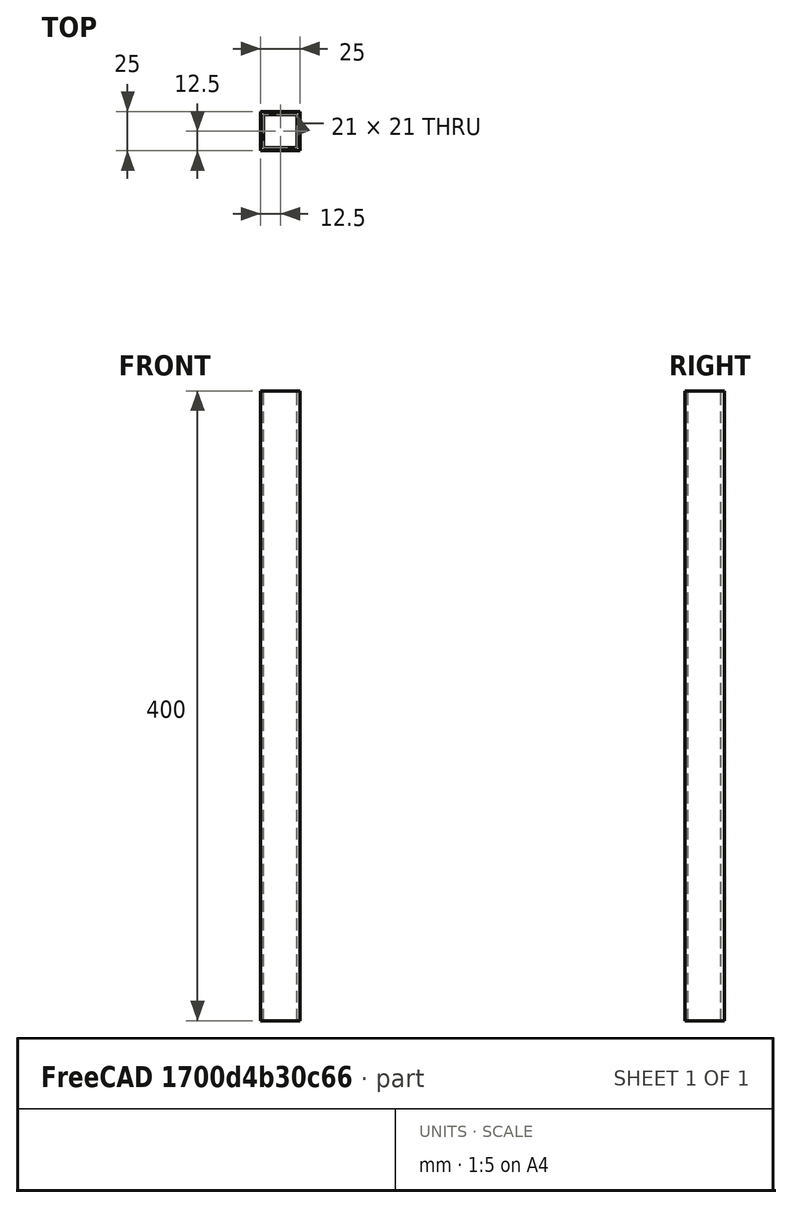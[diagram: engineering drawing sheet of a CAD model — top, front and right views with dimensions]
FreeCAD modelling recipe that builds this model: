
FCSTD DOCUMENT  (FreeCAD 0.21R33771 (Git))
Label: AluVierkantRohr 400mm
License: All rights reserved
LicenseURL: http://en.wikipedia.org/wiki/All_rights_reserved
objects: Sketcher::SketchObject×1, PartDesign::Pad×1, PartDesign::Body×1
note: 4 computed .brp shape members not serialized (recipe doc carries the construction recipe); baked Part::Feature solids carry a one-line shape summary decoded from their .brp

FEATURE [Sketcher::SketchObject] Sketch
  FullyConstrained = true
  MapMode = 5
  Support = -> [XY_Plane]
  sketch-geometry (8):
    g0: LineSegment StartX=0 StartY=0 StartZ=0 EndX=-25 EndY=0 EndZ=0
    g1: LineSegment StartX=-25 StartY=0 StartZ=0 EndX=-25 EndY=25 EndZ=0
    g2: LineSegment StartX=-25 StartY=25 StartZ=0 EndX=0 EndY=25 EndZ=0
    g3: LineSegment StartX=0 StartY=25 StartZ=0 EndX=0 EndY=0 EndZ=0
    g4: LineSegment StartX=-23 StartY=23 StartZ=0 EndX=-2 EndY=23 EndZ=0
    g5: LineSegment StartX=-2 StartY=23 StartZ=0 EndX=-2 EndY=2 EndZ=0
    g6: LineSegment StartX=-2 StartY=2 StartZ=0 EndX=-23 EndY=2 EndZ=0
    g7: LineSegment StartX=-23 StartY=2 StartZ=0 EndX=-23 EndY=23 EndZ=0
  constraints (23):
    c: Coincident(g0,g1)
    c: Coincident(g1,g2)
    c: Coincident(g2,g3)
    c: Coincident(g3,g0)
    c: Horizontal(g0)
    c: Horizontal(g2)
    c: Vertical(g1)
    c: Vertical(g3)
    c: Coincident(g0,g-1)
    c: Distance(g2) = 25
    c: Distance(g1) = 25
    c: Coincident(g4,g5)
    c: Coincident(g5,g6)
    c: Coincident(g6,g7)
    c: Coincident(g7,g4)
    c: Horizontal(g4)
    c: Horizontal(g6)
    c: Vertical(g5)
    c: Vertical(g7)
    c: Distance(g6,g1) = 2
    c: Distance(g5,g3) = 2
    c: Distance(g5,g0) = 2
    c: Distance(g4,g2) = 2
FEATURE [PartDesign::Pad] Pad
  Direction = (0,0,1)
  Length = 400
  Length2 = 10
  Profile = -> Sketch
  ReferenceAxis = -> Sketch [N_Axis]
  Type = 0
FEATURE [PartDesign::Body] Body  label="Körper"
  Group = -> [Sketch,Pad]
  Origin = -> Origin
  Tip = -> Pad
